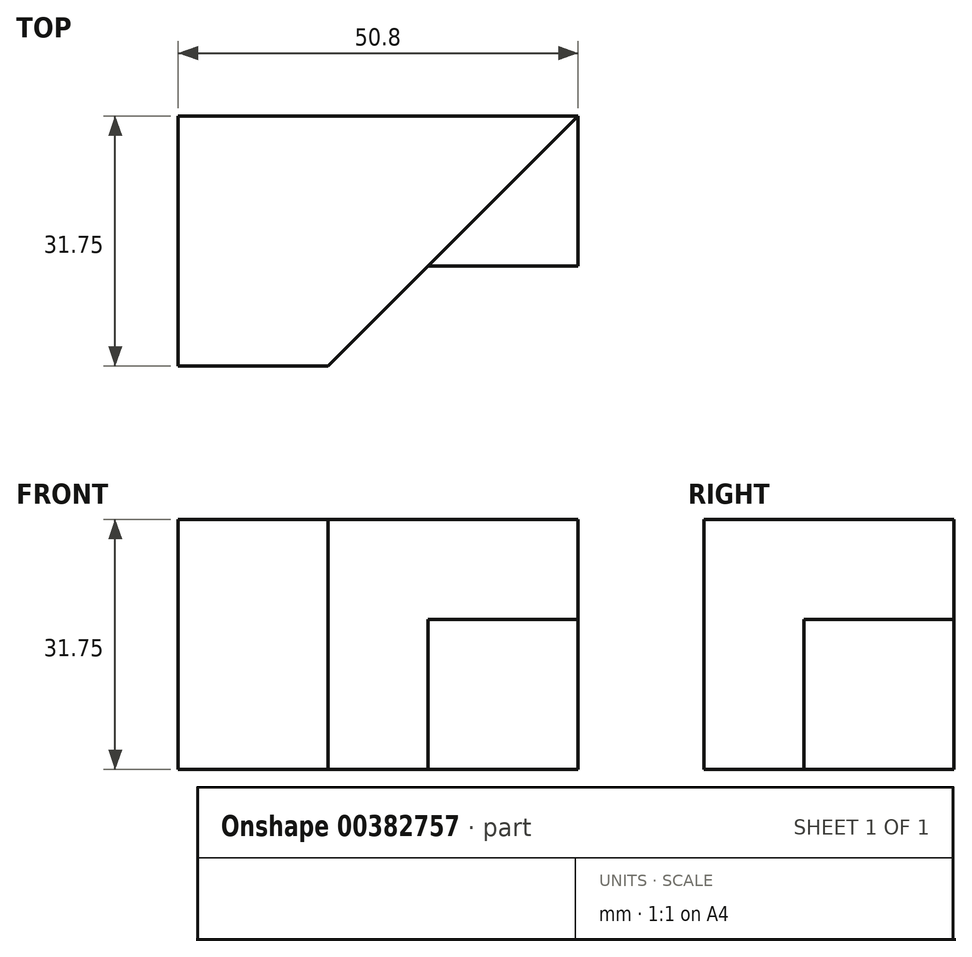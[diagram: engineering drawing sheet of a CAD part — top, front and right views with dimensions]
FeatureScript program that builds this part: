
annotation { "Feature Type Name" : "Feature", "Feature Type Description" : "" }
export const myFeature = defineFeature(function(context is Context, id is Id, definition is map)
    precondition{}
    {
        {
            var Q0;
            Q0=qCreatedBy(makeId("Front.planeOp"),FACE);
            var sketch = newSketch(context, id + "F0", { "sketchPlane" : qUnion([Q0])});
            skLineSegment(sketch, "E0", {"start": v(0, 0) * mm, "end": v(-50.8, 0) * mm});
            skLineSegment(sketch, "E1", {"start": v(-50.8, 0) * mm, "end": v(-50.8, 31.75) * mm});
            skLineSegment(sketch, "E2", {"start": v(-50.8, 31.75) * mm, "end": v(0, 31.75) * mm});
            skLineSegment(sketch, "E3", {"start": v(0, 31.75) * mm, "end": v(0, 0) * mm});
            skSolve(sketch);
        }
        {
            var Q0;
            Q0=makeQuery(id+"F0.imprint","IMPRINT",FACE,{"disambiguationData":[TD([[makeQuery(id+"F0.imprint","IMPRINT",EDGE,{"derivedFrom":sQuery(id+"F0.wireOp",EDGE,"E0")}),-1.0]])]});
            extrude(context, id + "F1", {"entities" : qUnion([Q0]), "depth" : 31.75 * mm});
        }
        {
            var Q0;
            Q0=makeQuery(id+"F1.opExtrude","SWEPT_FACE",FACE,{"disambiguationData":[OSD([sQuery(id+"F0.wireOp",EDGE,"E0")])]});
            var sketch = newSketch(context, id + "F2", { "sketchPlane" : qUnion([Q0])});
            skLineSegment(sketch, "E4", {"start": v(-31.75, 31.75) * mm, "end": v(0, 0) * mm});
            skSolve(sketch);
        }
        {
            var Q0;
            {var subQ0=sQuery(id+"F2.wireOp",EDGE,"E4");Q0=makeQuery(id+"F2.imprint","IMPRINT",FACE,{"disambiguationData":[TD([[makeQuery(id+"F2.imprint","IMPRINT",EDGE,{"derivedFrom":subQ0}),1.0]])]});}
            extrude(context, id + "F3", {"entities" : qUnion([Q0]), "operationType" : NewBodyOperationType.REMOVE, "oppositeDirection" : true, "depth" : 31.75 * mm});
        }
        {
            var Q0;
            Q0=makeQuery(id+"F1.opExtrude","SWEPT_FACE",FACE,{"disambiguationData":[OSD([sQuery(id+"F0.wireOp",EDGE,"E0")])]});
            var sketch = newSketch(context, id + "F4", { "sketchPlane" : qUnion([Q0])});
            skLineSegment(sketch, "E5", {"start": v(0, 0) * mm, "end": v(0, 19.05) * mm});
            skLineSegment(sketch, "E6", {"start": v(0, 19.05) * mm, "end": v(-19.05, 19.05) * mm});
            skLineSegment(sketch, "E7", {"start": v(-19.05, 19.05) * mm, "end": v(0, 0) * mm});
            skSolve(sketch);
        }
        {
            var Q0;
            Q0=makeQuery(id+"F4.imprint","IMPRINT",FACE,{"disambiguationData":[TD([[makeQuery(id+"F4.imprint","IMPRINT",EDGE,{"derivedFrom":sQuery(id+"F4.wireOp",EDGE,"E5")}),1.0]])]});
            extrude(context, id + "F5", {"entities" : qUnion([Q0]), "operationType" : NewBodyOperationType.ADD, "depth" : -19.05 * mm});
        }
    });
